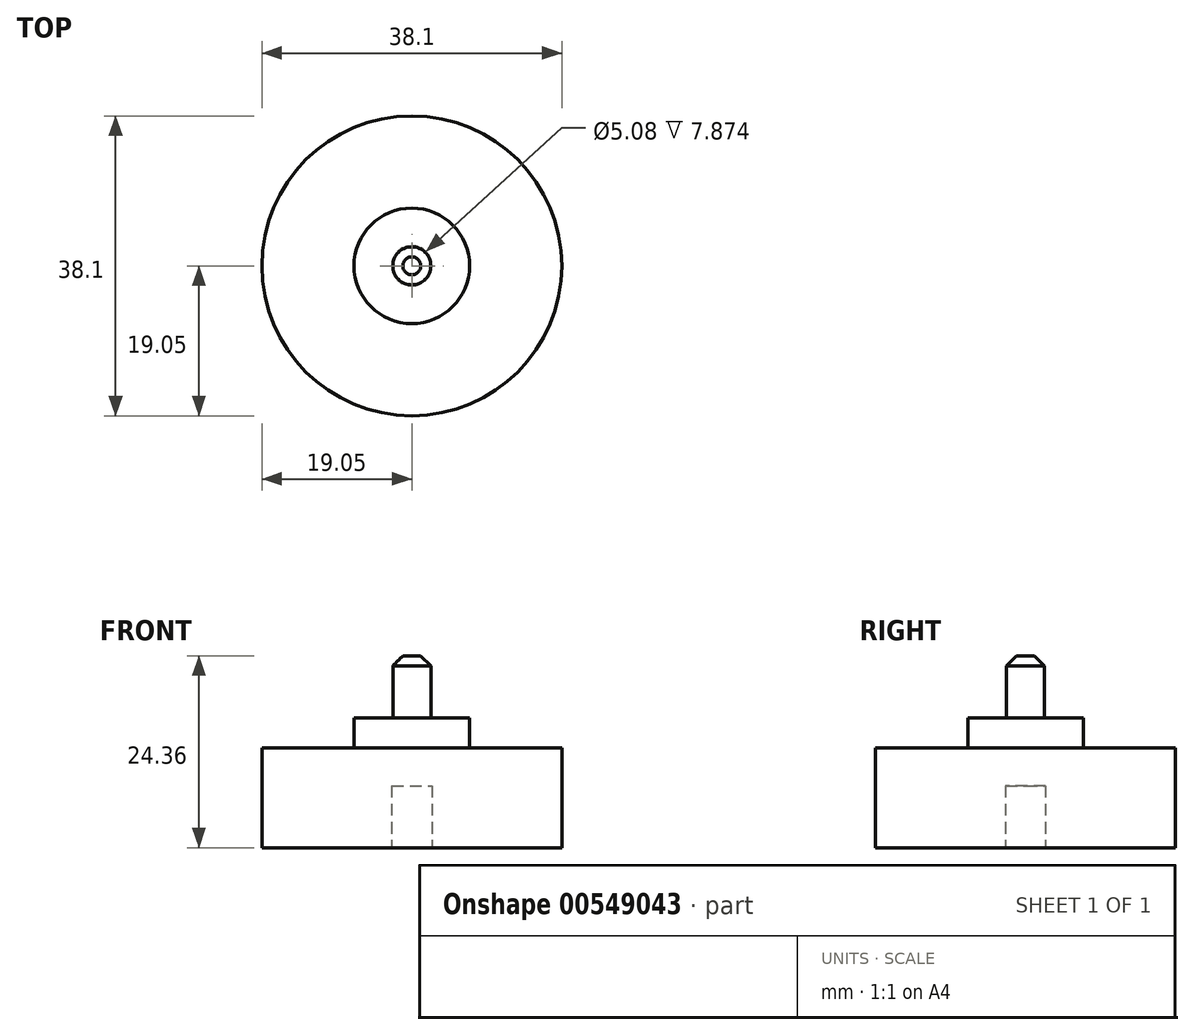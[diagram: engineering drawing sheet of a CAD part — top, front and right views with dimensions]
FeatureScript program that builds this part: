
annotation { "Feature Type Name" : "Feature", "Feature Type Description" : "" }
export const myFeature = defineFeature(function(context is Context, id is Id, definition is map)
    precondition{}
    {
        {
            var Q0;
            Q0=qCreatedBy(makeId("Front.planeOp"),FACE);
            var sketch = newSketch(context, id + "F0", { "sketchPlane" : qUnion([Q0])});
            skLineSegment(sketch, "E0", {"start": v(19.05, 0) * mm, "end": v(19.05, 12.7) * mm});
            skLineSegment(sketch, "E1", {"start": v(19.05, 12.7) * mm, "end": v(7.34, 12.7) * mm});
            skLineSegment(sketch, "E2", {"start": v(0, 12.7) * mm, "end": v(0, 16.51) * mm});
            skLineSegment(sketch, "E3", {"start": v(2.41, 16.51) * mm, "end": v(7.34, 16.51) * mm});
            skLineSegment(sketch, "E4", {"start": v(7.34, 16.51) * mm, "end": v(7.34, 12.7) * mm});
            skLineSegment(sketch, "E5", {"start": v(2.54, 0) * mm, "end": v(2.54, 7.87) * mm});
            skLineSegment(sketch, "E6", {"start": v(2.54, 7.87) * mm, "end": v(0, 7.87) * mm});
            skLineSegment(sketch, "E7", {"start": v(0, 7.87) * mm, "end": v(0, 12.7) * mm});
            skLineSegment(sketch, "E8", {"start": v(19.05, 0) * mm, "end": v(2.54, 0) * mm});
            skLineSegment(sketch, "E9", {"start": v(0, 16.51) * mm, "end": v(0, 24.36) * mm});
            skLineSegment(sketch, "E10", {"start": v(0, 24.36) * mm, "end": v(2.41, 24.36) * mm});
            skLineSegment(sketch, "E11", {"start": v(2.41, 24.36) * mm, "end": v(2.41, 16.51) * mm});
            skSolve(sketch);
        }
        {
            var Q0;
            Q0 = qSketchRegion(id + "F0", true);
            var Q1;
            Q1=sQuery(id+"F0.wireOp",EDGE,"E2");
            revolve(context, id + "F1", {"entities" : qUnion([Q0]), "axis" : qUnion([Q1]), "revolveType" : RevolveType.FULL});
        }
        {
            var Q0;
            Q0=makeQuery(id+"F1.opRevolve","SWEPT_EDGE",EDGE,{"disambiguationData":[OSD([sQuery(id+"F0.wireOp",EDGE,"E10"),sQuery(id+"F0.wireOp",EDGE,"E11")])]});
            chamfer(context, id + "F2", {"entities" : qUnion([Q0]), "width" : 1.27 * mm, "tangentPropagation" : true});
        }
    });
